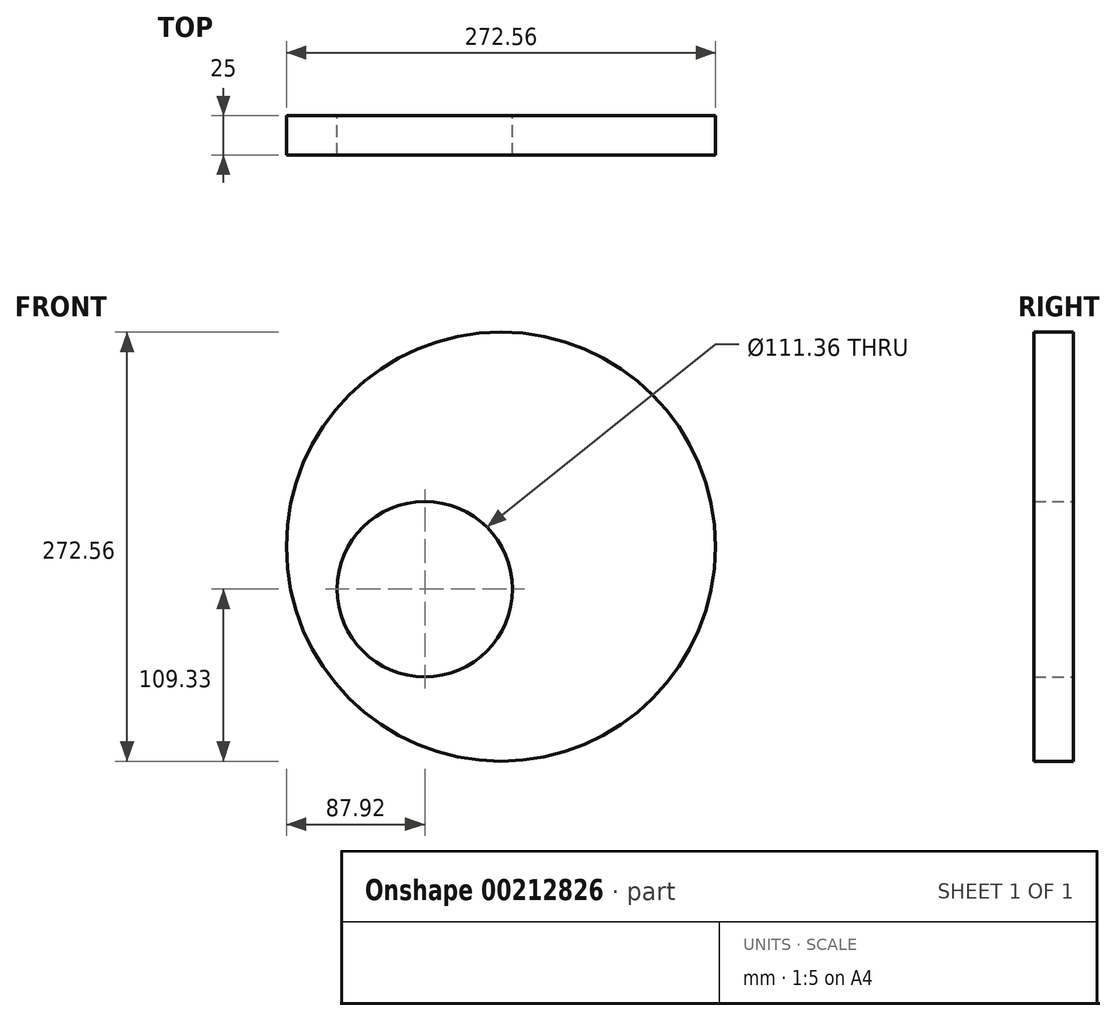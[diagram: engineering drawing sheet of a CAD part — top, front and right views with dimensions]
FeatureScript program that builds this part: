
annotation { "Feature Type Name" : "Feature", "Feature Type Description" : "" }
export const myFeature = defineFeature(function(context is Context, id is Id, definition is map)
    precondition{}
    {
        {
            var Q0;
            Q0=qCreatedBy(makeId("Front.planeOp"),FACE);
            var sketch = newSketch(context, id + "F0", { "sketchPlane" : qUnion([Q0])});
            skCircle(sketch, "E0", {"center": v(0, 0) * mm, "radius": 55.68 * mm});
            skCircle(sketch, "E1", {"center": v(48.36, 26.95) * mm, "radius": 136.28 * mm});
            skSolve(sketch);
        }
        {
            var Q0;
            Q0=makeQuery(id+"F0.imprint","IMPRINT",FACE,{"disambiguationData":[TD([[makeQuery(id+"F0.imprint","IMPRINT",EDGE,{"derivedFrom":sQuery(id+"F0.wireOp",EDGE,"E0")}),-1.0]])]});
            extrude(context, id + "F1", {"entities" : qUnion([Q0]), "depth" : 25 * mm, "offsetDistance" : 25 * mm});
        }
    });
